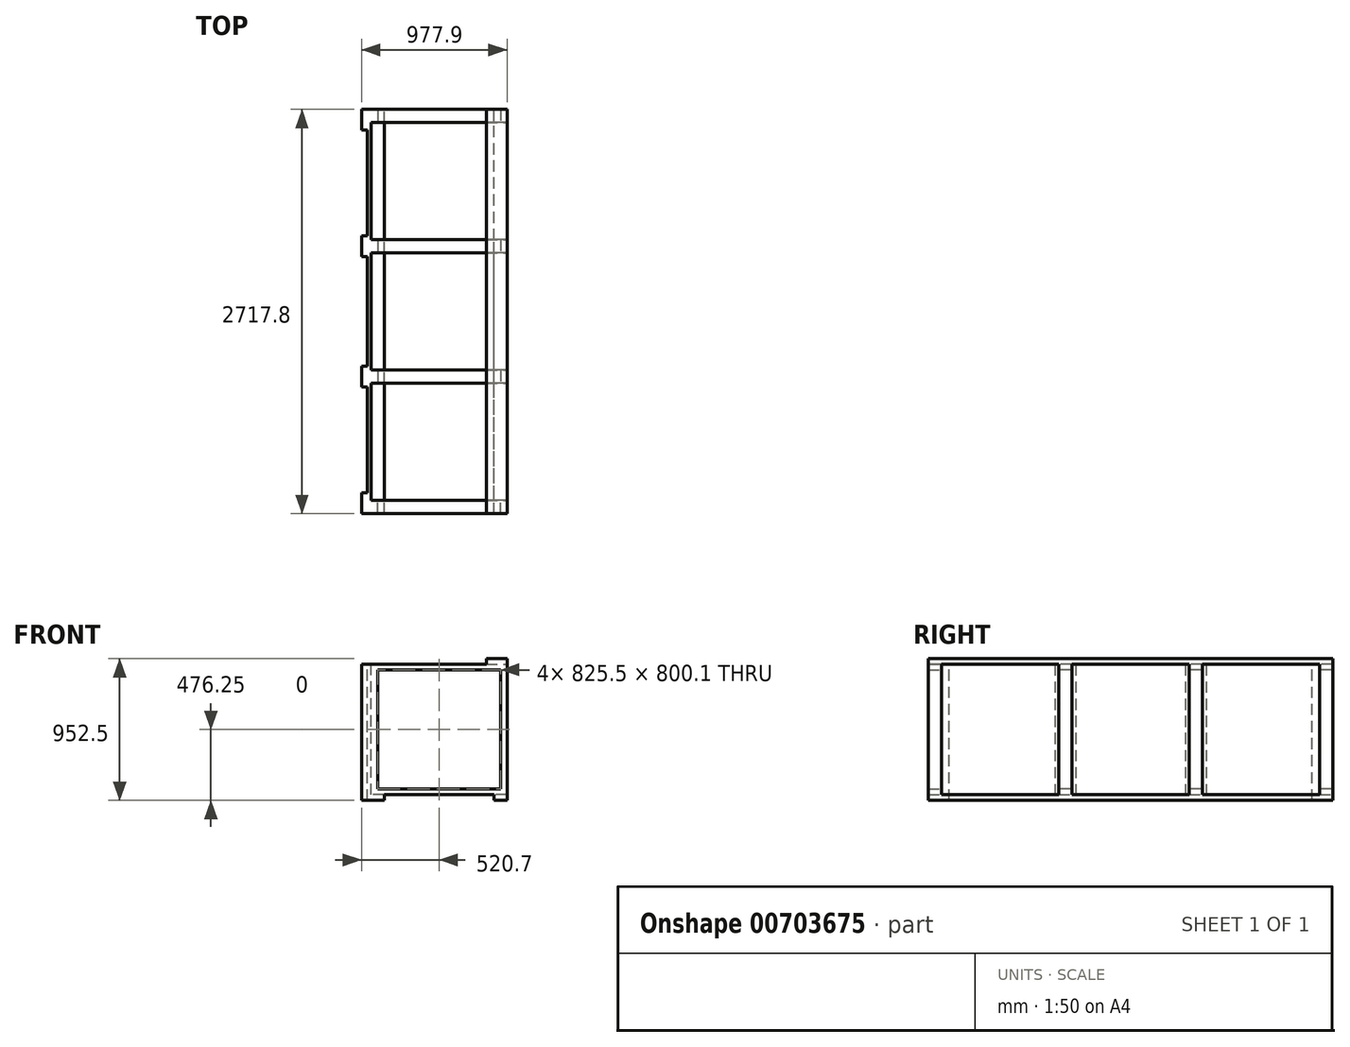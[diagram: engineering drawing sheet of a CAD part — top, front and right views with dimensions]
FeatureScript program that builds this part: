
annotation { "Feature Type Name" : "Feature", "Feature Type Description" : "" }
export const myFeature = defineFeature(function(context is Context, id is Id, definition is map)
    precondition{}
    {
        {
            var Q0;
            Q0=qCreatedBy(makeId("Front.planeOp"),FACE);
            var sketch = newSketch(context, id + "F0", { "sketchPlane" : qUnion([Q0])});
            skLineSegment(sketch, "E0.bottom", {"start": v(0, 0) * mm, "end": v(88.9, 0) * mm});
            skLineSegment(sketch, "E0.top", {"start": v(0, 76.2) * mm, "end": v(914.4, 76.2) * mm});
            skLineSegment(sketch, "E0.left", {"start": v(0, 0) * mm, "end": v(0, 76.2) * mm});
            skLineSegment(sketch, "E0.right", {"start": v(914.4, 0) * mm, "end": v(914.4, 76.2) * mm});
            skLineSegment(sketch, "E1.top", {"start": v(88.9, 38.1) * mm, "end": v(825.5, 38.1) * mm});
            skLineSegment(sketch, "E1.left", {"start": v(88.9, 0) * mm, "end": v(88.9, 38.1) * mm});
            skLineSegment(sketch, "E1.right", {"start": v(825.5, 0) * mm, "end": v(825.5, 38.1) * mm});
            skLineSegment(sketch, "E2.trimOffspring", {"start": v(825.5, 0) * mm, "end": v(914.4, 0) * mm});
            skSolve(sketch);
        }
        {
            var Q0;
            Q0=makeQuery(id+"F0.imprint","IMPRINT",FACE,{"disambiguationData":[TD([[makeQuery(id+"F0.imprint","IMPRINT",EDGE,{"derivedFrom":sQuery(id+"F0.wireOp",EDGE,"E0.bottom")}),1.0]])]});
            extrude(context, id + "F1", {"entities" : qUnion([Q0]), "depth" : 2717.8 * mm, "offsetDistance" : 25.4 * mm});
        }
        {
            var Q0;
            Q0=makeQuery(id+"F1.opExtrude","SWEPT_FACE",FACE,{"disambiguationData":[OSD([sQuery(id+"F0.wireOp",EDGE,"E0.top")])]});
            var sketch = newSketch(context, id + "F2", { "sketchPlane" : qUnion([Q0])});
            skLineSegment(sketch, "E3.bottom", {"start": v(914.4, -2628.9) * mm, "end": v(0, -2628.9) * mm});
            skLineSegment(sketch, "E3.top", {"start": v(914.4, -1841.5) * mm, "end": v(0, -1841.5) * mm});
            skLineSegment(sketch, "E3.left", {"start": v(914.4, -2628.9) * mm, "end": v(914.4, -1841.5) * mm});
            skLineSegment(sketch, "E3.right", {"start": v(0, -2628.9) * mm, "end": v(0, -1841.5) * mm});
            skLineSegment(sketch, "E4.bottom", {"start": v(914.4, -88.9) * mm, "end": v(0, -88.9) * mm});
            skLineSegment(sketch, "E4.top", {"start": v(914.4, -876.3) * mm, "end": v(0, -876.3) * mm});
            skLineSegment(sketch, "E4.left", {"start": v(914.4, -88.9) * mm, "end": v(914.4, -876.3) * mm});
            skLineSegment(sketch, "E4.right", {"start": v(0, -88.9) * mm, "end": v(0, -876.3) * mm});
            skLineSegment(sketch, "E5.bottom", {"start": v(914.4, -1752.6) * mm, "end": v(0, -1752.6) * mm});
            skLineSegment(sketch, "E5.top", {"start": v(914.4, -965.2) * mm, "end": v(0, -965.2) * mm});
            skLineSegment(sketch, "E5.left", {"start": v(914.4, -1752.6) * mm, "end": v(914.4, -965.2) * mm});
            skLineSegment(sketch, "E5.right", {"start": v(0, -1752.6) * mm, "end": v(0, -965.2) * mm});
            skSolve(sketch);
        }
        {
            var Q0;
            Q0=makeQuery(id+"F2.imprint","IMPRINT",FACE,{"disambiguationData":[TD([[makeQuery(id+"F2.imprint","IMPRINT",EDGE,{"derivedFrom":sQuery(id+"F2.wireOp",EDGE,"E3.bottom")}),-1.0]])]});
            var Q1;
            Q1=makeQuery(id+"F2.imprint","IMPRINT",FACE,{"disambiguationData":[TD([[makeQuery(id+"F2.imprint","IMPRINT",EDGE,{"derivedFrom":sQuery(id+"F2.wireOp",EDGE,"E5.bottom")}),-1.0]])]});
            var Q2;
            Q2=makeQuery(id+"F2.imprint","IMPRINT",FACE,{"disambiguationData":[TD([[makeQuery(id+"F2.imprint","IMPRINT",EDGE,{"derivedFrom":sQuery(id+"F2.wireOp",EDGE,"E4.bottom")}),1.0]])]});
            extrude(context, id + "F3", {"entities" : qUnion([Q0, Q1, Q2]), "operationType" : NewBodyOperationType.REMOVE, "oppositeDirection" : true, "depth" : 38.1 * mm, "offsetDistance" : 25.4 * mm});
        }
        {
            var Q0;
            {var subQ2=sQuery(id+"F0.wireOp",EDGE,"E0.top");Q0=makeQuery(id+"F3.boolean.opBoolean","SPLIT",FACE,{"disambiguationData":[TD([makeQuery(id+"F3.opExtrude","SWEPT_FACE",FACE,{"disambiguationData":[OSD([sQuery(id+"F2.wireOp",EDGE,"E4.bottom")])]})])],"derivedFrom":makeQuery(id+"F1.opExtrude","SWEPT_FACE",FACE,{"disambiguationData":[OSD([subQ2])]})});}
            var sketch = newSketch(context, id + "F4", { "sketchPlane" : qUnion([Q0])});
            skLineSegment(sketch, "E6", {"start": v(0, 0) * mm, "end": v(0, -2717.8) * mm, "construction": true});
            skLineSegment(sketch, "E7", {"start": v(914.4, 0) * mm, "end": v(914.4, -2717.8) * mm, "construction": true});
            skLineSegment(sketch, "E8", {"start": v(88.9, 0) * mm, "end": v(88.9, -2717.8) * mm, "construction": true});
            skLineSegment(sketch, "E9", {"start": v(825.5, 0) * mm, "end": v(825.5, -2717.8) * mm, "construction": true});
            skLineSegment(sketch, "E10.bottom", {"start": v(0, 0) * mm, "end": v(44.45, 0) * mm});
            skLineSegment(sketch, "E10.top", {"start": v(0, -88.9) * mm, "end": v(44.45, -88.9) * mm});
            skLineSegment(sketch, "E10.left", {"start": v(0, 0) * mm, "end": v(0, -88.9) * mm});
            skLineSegment(sketch, "E10.right", {"start": v(44.45, 0) * mm, "end": v(44.45, -88.9) * mm});
            skLineSegment(sketch, "E11.bottom", {"start": v(914.4, 0) * mm, "end": v(869.95, 0) * mm});
            skLineSegment(sketch, "E11.top", {"start": v(914.4, -88.9) * mm, "end": v(869.95, -88.9) * mm});
            skLineSegment(sketch, "E11.left", {"start": v(914.4, 0) * mm, "end": v(914.4, -88.9) * mm});
            skLineSegment(sketch, "E11.right", {"start": v(869.95, 0) * mm, "end": v(869.95, -88.9) * mm});
            skLineSegment(sketch, "E12", {"start": v(0, -2717.8) * mm, "end": v(914.4, -2717.8) * mm, "construction": true});
            skLineSegment(sketch, "E13", {"start": v(0, -2628.9) * mm, "end": v(914.4, -2628.9) * mm, "construction": true});
            skLineSegment(sketch, "E14", {"start": v(0, -1841.5) * mm, "end": v(914.4, -1841.5) * mm, "construction": true});
            skLineSegment(sketch, "E15", {"start": v(0, -1752.6) * mm, "end": v(914.4, -1752.6) * mm, "construction": true});
            skLineSegment(sketch, "E16", {"start": v(0, -965.2) * mm, "end": v(914.4, -965.2) * mm, "construction": true});
            skLineSegment(sketch, "E17", {"start": v(0, -876.3) * mm, "end": v(914.4, -876.3) * mm, "construction": true});
            skLineSegment(sketch, "E18.bottom", {"start": v(0, -876.3) * mm, "end": v(44.45, -876.3) * mm});
            skLineSegment(sketch, "E18.top", {"start": v(0, -965.2) * mm, "end": v(44.45, -965.2) * mm});
            skLineSegment(sketch, "E18.left", {"start": v(0, -876.3) * mm, "end": v(0, -965.2) * mm});
            skLineSegment(sketch, "E18.right", {"start": v(44.45, -876.3) * mm, "end": v(44.45, -965.2) * mm});
            skLineSegment(sketch, "E19.bottom", {"start": v(914.4, -876.3) * mm, "end": v(869.95, -876.3) * mm});
            skLineSegment(sketch, "E19.top", {"start": v(914.4, -965.2) * mm, "end": v(869.95, -965.2) * mm});
            skLineSegment(sketch, "E19.left", {"start": v(914.4, -876.3) * mm, "end": v(914.4, -965.2) * mm});
            skLineSegment(sketch, "E19.right", {"start": v(869.95, -876.3) * mm, "end": v(869.95, -965.2) * mm});
            skLineSegment(sketch, "E20.bottom", {"start": v(0, -1752.6) * mm, "end": v(44.45, -1752.6) * mm});
            skLineSegment(sketch, "E20.top", {"start": v(0, -1841.5) * mm, "end": v(44.45, -1841.5) * mm});
            skLineSegment(sketch, "E20.left", {"start": v(0, -1752.6) * mm, "end": v(0, -1841.5) * mm});
            skLineSegment(sketch, "E20.right", {"start": v(44.45, -1752.6) * mm, "end": v(44.45, -1841.5) * mm});
            skLineSegment(sketch, "E21.bottom", {"start": v(914.4, -1752.6) * mm, "end": v(869.95, -1752.6) * mm});
            skLineSegment(sketch, "E21.top", {"start": v(914.4, -1841.5) * mm, "end": v(869.95, -1841.5) * mm});
            skLineSegment(sketch, "E21.left", {"start": v(914.4, -1752.6) * mm, "end": v(914.4, -1841.5) * mm});
            skLineSegment(sketch, "E21.right", {"start": v(869.95, -1752.6) * mm, "end": v(869.95, -1841.5) * mm});
            skLineSegment(sketch, "E22.bottom", {"start": v(0, -2717.8) * mm, "end": v(44.45, -2717.8) * mm});
            skLineSegment(sketch, "E22.top", {"start": v(0, -2628.9) * mm, "end": v(44.45, -2628.9) * mm});
            skLineSegment(sketch, "E22.left", {"start": v(0, -2717.8) * mm, "end": v(0, -2628.9) * mm});
            skLineSegment(sketch, "E22.right", {"start": v(44.45, -2717.8) * mm, "end": v(44.45, -2628.9) * mm});
            skLineSegment(sketch, "E23.bottom", {"start": v(914.4, -2717.8) * mm, "end": v(869.95, -2717.8) * mm});
            skLineSegment(sketch, "E23.top", {"start": v(914.4, -2628.9) * mm, "end": v(869.95, -2628.9) * mm});
            skLineSegment(sketch, "E23.left", {"start": v(914.4, -2717.8) * mm, "end": v(914.4, -2628.9) * mm});
            skLineSegment(sketch, "E23.right", {"start": v(869.95, -2717.8) * mm, "end": v(869.95, -2628.9) * mm});
            skSolve(sketch);
        }
        {
            var Q0;
            Q0=makeQuery(id+"F4.imprint","IMPRINT",FACE,{"disambiguationData":[TD([[makeQuery(id+"F4.imprint","IMPRINT",EDGE,{"derivedFrom":sQuery(id+"F4.wireOp",EDGE,"E11.bottom")}),-1.0]])]});
            var Q1;
            Q1=makeQuery(id+"F4.imprint","IMPRINT",FACE,{"disambiguationData":[TD([[makeQuery(id+"F4.imprint","IMPRINT",EDGE,{"derivedFrom":sQuery(id+"F4.wireOp",EDGE,"E10.bottom")}),-1.0]])]});
            var Q2;
            Q2=makeQuery(id+"F4.imprint","IMPRINT",FACE,{"disambiguationData":[TD([[makeQuery(id+"F4.imprint","IMPRINT",EDGE,{"derivedFrom":sQuery(id+"F4.wireOp",EDGE,"E18.bottom")}),-1.0]])]});
            var Q3;
            Q3=makeQuery(id+"F4.imprint","IMPRINT",FACE,{"disambiguationData":[TD([[makeQuery(id+"F4.imprint","IMPRINT",EDGE,{"derivedFrom":sQuery(id+"F4.wireOp",EDGE,"E19.bottom")}),1.0]])]});
            var Q4;
            Q4=makeQuery(id+"F4.imprint","IMPRINT",FACE,{"disambiguationData":[TD([[makeQuery(id+"F4.imprint","IMPRINT",EDGE,{"derivedFrom":sQuery(id+"F4.wireOp",EDGE,"E21.bottom")}),1.0]])]});
            var Q5;
            Q5=makeQuery(id+"F4.imprint","IMPRINT",FACE,{"disambiguationData":[TD([[makeQuery(id+"F4.imprint","IMPRINT",EDGE,{"derivedFrom":sQuery(id+"F4.wireOp",EDGE,"E20.bottom")}),-1.0]])]});
            var Q6;
            Q6=makeQuery(id+"F4.imprint","IMPRINT",FACE,{"disambiguationData":[TD([[makeQuery(id+"F4.imprint","IMPRINT",EDGE,{"derivedFrom":sQuery(id+"F4.wireOp",EDGE,"E22.bottom")}),1.0]])]});
            var Q7;
            Q7=makeQuery(id+"F4.imprint","IMPRINT",FACE,{"disambiguationData":[TD([[makeQuery(id+"F4.imprint","IMPRINT",EDGE,{"derivedFrom":sQuery(id+"F4.wireOp",EDGE,"E23.bottom")}),-1.0]])]});
            extrude(context, id + "F5", {"entities" : qUnion([Q0, Q1, Q2, Q3, Q4, Q5, Q6, Q7]), "operationType" : NewBodyOperationType.ADD, "depth" : 800.1 * mm, "offsetDistance" : 25.4 * mm});
        }
        {
            var Q0;
            Q0=makeQuery(id+"F5.boolean.opBoolean","MERGE",FACE,{"derivedFrom":[makeQuery(id+"F1.opExtrude","SWEPT_FACE",FACE,{"disambiguationData":[OSD([sQuery(id+"F0.wireOp",EDGE,"E0.right")])]}),makeQuery(id+"F5.opExtrude","SWEPT_FACE",FACE,{"disambiguationData":[OSD([sQuery(id+"F4.wireOp",EDGE,"E11.left")])]}),makeQuery(id+"F5.opExtrude","SWEPT_FACE",FACE,{"disambiguationData":[OSD([sQuery(id+"F4.wireOp",EDGE,"E19.left")])]}),makeQuery(id+"F5.opExtrude","SWEPT_FACE",FACE,{"disambiguationData":[OSD([sQuery(id+"F4.wireOp",EDGE,"E21.left")])]}),makeQuery(id+"F5.opExtrude","SWEPT_FACE",FACE,{"disambiguationData":[OSD([sQuery(id+"F4.wireOp",EDGE,"E23.left")])]})]});
            var sketch = newSketch(context, id + "F6", { "sketchPlane" : qUnion([Q0])});
            skLineSegment(sketch, "E24.bottom", {"start": v(-2717.8, 876.3) * mm, "end": v(-2628.9, 876.3) * mm});
            skLineSegment(sketch, "E24.top", {"start": v(-2717.8, 914.4) * mm, "end": v(-2628.9, 914.4) * mm});
            skLineSegment(sketch, "E24.left", {"start": v(-2717.8, 876.3) * mm, "end": v(-2717.8, 914.4) * mm});
            skLineSegment(sketch, "E24.right", {"start": v(-2628.9, 876.3) * mm, "end": v(-2628.9, 914.4) * mm});
            skLineSegment(sketch, "E25.bottom", {"start": v(-1841.5, 876.3) * mm, "end": v(-1752.6, 876.3) * mm});
            skLineSegment(sketch, "E25.top", {"start": v(-1841.5, 914.4) * mm, "end": v(-1752.6, 914.4) * mm});
            skLineSegment(sketch, "E25.left", {"start": v(-1841.5, 876.3) * mm, "end": v(-1841.5, 914.4) * mm});
            skLineSegment(sketch, "E25.right", {"start": v(-1752.6, 876.3) * mm, "end": v(-1752.6, 914.4) * mm});
            skLineSegment(sketch, "E26.bottom", {"start": v(-965.2, 876.3) * mm, "end": v(-876.3, 876.3) * mm});
            skLineSegment(sketch, "E26.top", {"start": v(-965.2, 914.4) * mm, "end": v(-876.3, 914.4) * mm});
            skLineSegment(sketch, "E26.left", {"start": v(-965.2, 876.3) * mm, "end": v(-965.2, 914.4) * mm});
            skLineSegment(sketch, "E26.right", {"start": v(-876.3, 876.3) * mm, "end": v(-876.3, 914.4) * mm});
            skLineSegment(sketch, "E27.bottom", {"start": v(-88.9, 876.3) * mm, "end": v(0, 876.3) * mm});
            skLineSegment(sketch, "E27.top", {"start": v(-88.9, 914.4) * mm, "end": v(0, 914.4) * mm});
            skLineSegment(sketch, "E27.left", {"start": v(-88.9, 876.3) * mm, "end": v(-88.9, 914.4) * mm});
            skLineSegment(sketch, "E27.right", {"start": v(0, 876.3) * mm, "end": v(0, 914.4) * mm});
            skSolve(sketch);
        }
        {
            var Q0;
            Q0=makeQuery(id+"F6.imprint","IMPRINT",FACE,{"disambiguationData":[TD([[makeQuery(id+"F6.imprint","IMPRINT",EDGE,{"derivedFrom":sQuery(id+"F6.wireOp",EDGE,"E24.bottom")}),1.0]])]});
            var Q1;
            Q1=makeQuery(id+"F6.imprint","IMPRINT",FACE,{"disambiguationData":[TD([[makeQuery(id+"F6.imprint","IMPRINT",EDGE,{"derivedFrom":sQuery(id+"F6.wireOp",EDGE,"E25.bottom")}),-1.0]])]});
            var Q2;
            Q2=makeQuery(id+"F6.imprint","IMPRINT",FACE,{"disambiguationData":[TD([[makeQuery(id+"F6.imprint","IMPRINT",EDGE,{"derivedFrom":sQuery(id+"F6.wireOp",EDGE,"E26.bottom")}),-1.0]])]});
            var Q3;
            Q3=makeQuery(id+"F6.imprint","IMPRINT",FACE,{"disambiguationData":[TD([[makeQuery(id+"F6.imprint","IMPRINT",EDGE,{"derivedFrom":sQuery(id+"F6.wireOp",EDGE,"E27.bottom")}),1.0]])]});
            extrude(context, id + "F7", {"entities" : qUnion([Q0, Q1, Q2, Q3]), "operationType" : NewBodyOperationType.ADD, "oppositeDirection" : true, "depth" : 914.4 * mm, "offsetDistance" : 25.4 * mm});
        }
        {
            var Q0;
            Q0=makeQuery(id+"F7.boolean.opBoolean","MERGE",FACE,{"derivedFrom":[makeQuery(id+"F5.boolean.opBoolean","MERGE",FACE,{"derivedFrom":[makeQuery(id+"F1.opExtrude","CAP_FACE",FACE,{"disambiguationData":[OSD([sQuery(id+"F0.wireOp",EDGE,"E0.bottom"),sQuery(id+"F0.wireOp",EDGE,"E0.top"),sQuery(id+"F0.wireOp",EDGE,"E0.left"),sQuery(id+"F0.wireOp",EDGE,"E0.right"),sQuery(id+"F0.wireOp",EDGE,"E1.top"),sQuery(id+"F0.wireOp",EDGE,"E1.left"),sQuery(id+"F0.wireOp",EDGE,"E1.right"),sQuery(id+"F0.wireOp",EDGE,"E2.trimOffspring")])],"isStart":false}),makeQuery(id+"F5.opExtrude","SWEPT_FACE",FACE,{"disambiguationData":[OSD([sQuery(id+"F4.wireOp",EDGE,"E22.bottom")])]}),makeQuery(id+"F5.opExtrude","SWEPT_FACE",FACE,{"disambiguationData":[OSD([sQuery(id+"F4.wireOp",EDGE,"E23.bottom")])]})]}),makeQuery(id+"F7.opExtrude","SWEPT_FACE",FACE,{"disambiguationData":[OSD([sQuery(id+"F6.wireOp",EDGE,"E24.left")])]})]});
            var sketch = newSketch(context, id + "F8", { "sketchPlane" : qUnion([Q0])});
            skLineSegment(sketch, "E28.bottom", {"start": v(914.4, 914.4) * mm, "end": v(774.7, 914.4) * mm});
            skLineSegment(sketch, "E28.top", {"start": v(914.4, 952.5) * mm, "end": v(774.7, 952.5) * mm});
            skLineSegment(sketch, "E28.left", {"start": v(914.4, 914.4) * mm, "end": v(914.4, 952.5) * mm});
            skLineSegment(sketch, "E28.right", {"start": v(774.7, 914.4) * mm, "end": v(774.7, 952.5) * mm});
            skSolve(sketch);
        }
        {
            var Q0;
            Q0=makeQuery(id+"F8.imprint","IMPRINT",FACE,{"disambiguationData":[TD([[makeQuery(id+"F8.imprint","IMPRINT",EDGE,{"derivedFrom":sQuery(id+"F8.wireOp",EDGE,"E28.bottom")}),1.0]])]});
            extrude(context, id + "F9", {"entities" : qUnion([Q0]), "operationType" : NewBodyOperationType.ADD, "oppositeDirection" : true, "depth" : 2717.8 * mm, "offsetDistance" : 25.4 * mm});
        }
        {
            var Q0;
            Q0=makeQuery(id+"F7.boolean.opBoolean","MERGE",FACE,{"derivedFrom":[makeQuery(id+"F5.boolean.opBoolean","MERGE",FACE,{"derivedFrom":[makeQuery(id+"F1.opExtrude","SWEPT_FACE",FACE,{"disambiguationData":[OSD([sQuery(id+"F0.wireOp",EDGE,"E0.left")])]}),makeQuery(id+"F5.opExtrude","SWEPT_FACE",FACE,{"disambiguationData":[OSD([sQuery(id+"F4.wireOp",EDGE,"E10.left")])]}),makeQuery(id+"F5.opExtrude","SWEPT_FACE",FACE,{"disambiguationData":[OSD([sQuery(id+"F4.wireOp",EDGE,"E18.left")])]}),makeQuery(id+"F5.opExtrude","SWEPT_FACE",FACE,{"disambiguationData":[OSD([sQuery(id+"F4.wireOp",EDGE,"E20.left")])]}),makeQuery(id+"F5.opExtrude","SWEPT_FACE",FACE,{"disambiguationData":[OSD([sQuery(id+"F4.wireOp",EDGE,"E22.left")])]})]}),makeQuery(id+"F7.opExtrude","CAP_FACE",FACE,{"disambiguationData":[OSD([sQuery(id+"F6.wireOp",EDGE,"E24.bottom"),sQuery(id+"F6.wireOp",EDGE,"E24.top"),sQuery(id+"F6.wireOp",EDGE,"E24.left"),sQuery(id+"F6.wireOp",EDGE,"E24.right")])],"isStart":false}),makeQuery(id+"F7.opExtrude","CAP_FACE",FACE,{"disambiguationData":[OSD([sQuery(id+"F6.wireOp",EDGE,"E25.bottom"),sQuery(id+"F6.wireOp",EDGE,"E25.top"),sQuery(id+"F6.wireOp",EDGE,"E25.left"),sQuery(id+"F6.wireOp",EDGE,"E25.right")])],"isStart":false}),makeQuery(id+"F7.opExtrude","CAP_FACE",FACE,{"disambiguationData":[OSD([sQuery(id+"F6.wireOp",EDGE,"E26.bottom"),sQuery(id+"F6.wireOp",EDGE,"E26.top"),sQuery(id+"F6.wireOp",EDGE,"E26.left"),sQuery(id+"F6.wireOp",EDGE,"E26.right")])],"isStart":false}),makeQuery(id+"F7.opExtrude","CAP_FACE",FACE,{"disambiguationData":[OSD([sQuery(id+"F6.wireOp",EDGE,"E27.bottom"),sQuery(id+"F6.wireOp",EDGE,"E27.top"),sQuery(id+"F6.wireOp",EDGE,"E27.left"),sQuery(id+"F6.wireOp",EDGE,"E27.right")])],"isStart":false})]});
            var sketch = newSketch(context, id + "F10", { "sketchPlane" : qUnion([Q0])});
            skLineSegment(sketch, "E29.bottom", {"start": v(0, 0) * mm, "end": v(139.7, 0) * mm});
            skLineSegment(sketch, "E29.top", {"start": v(0, 914.4) * mm, "end": v(139.7, 914.4) * mm});
            skLineSegment(sketch, "E29.left", {"start": v(0, 0) * mm, "end": v(0, 914.4) * mm});
            skLineSegment(sketch, "E29.right", {"start": v(139.7, 0) * mm, "end": v(139.7, 914.4) * mm});
            skLineSegment(sketch, "E30.bottom", {"start": v(2717.8, 0) * mm, "end": v(2578.1, 0) * mm});
            skLineSegment(sketch, "E30.top", {"start": v(2717.8, 914.4) * mm, "end": v(2578.1, 914.4) * mm});
            skLineSegment(sketch, "E30.left", {"start": v(2717.8, 0) * mm, "end": v(2717.8, 914.4) * mm});
            skLineSegment(sketch, "E30.right", {"start": v(2578.1, 0) * mm, "end": v(2578.1, 914.4) * mm});
            skLineSegment(sketch, "E31.bottom", {"start": v(850.9, 914.4) * mm, "end": v(990.6, 914.4) * mm});
            skLineSegment(sketch, "E31.top", {"start": v(850.9, 0) * mm, "end": v(990.6, 0) * mm});
            skLineSegment(sketch, "E31.left", {"start": v(850.9, 914.4) * mm, "end": v(850.9, 0) * mm});
            skLineSegment(sketch, "E31.right", {"start": v(990.6, 914.4) * mm, "end": v(990.6, 0) * mm});
            skLineSegment(sketch, "E32.bottom", {"start": v(1727.2, 914.4) * mm, "end": v(1866.9, 914.4) * mm});
            skLineSegment(sketch, "E32.top", {"start": v(1727.2, 0) * mm, "end": v(1866.9, 0) * mm});
            skLineSegment(sketch, "E32.left", {"start": v(1727.2, 914.4) * mm, "end": v(1727.2, 0) * mm});
            skLineSegment(sketch, "E32.right", {"start": v(1866.9, 914.4) * mm, "end": v(1866.9, 0) * mm});
            skSolve(sketch);
        }
        {
            var Q0;
            Q0 = qSketchRegion(id + "F10", true);
            extrude(context, id + "F11", {"entities" : qUnion([Q0]), "operationType" : NewBodyOperationType.ADD, "depth" : 63.5 * mm, "offsetDistance" : 25.4 * mm});
        }
        {
            var Q0;
            Q0=makeQuery(id+"F11.boolean.opBoolean","MERGE",FACE,{"derivedFrom":[makeQuery(id+"F7.opExtrude","SWEPT_FACE",FACE,{"disambiguationData":[OSD([sQuery(id+"F6.wireOp",EDGE,"E27.top")])]}),makeQuery(id+"F11.opExtrude","SWEPT_FACE",FACE,{"disambiguationData":[OSD([sQuery(id+"F10.wireOp",EDGE,"E29.top")])]})]});
            var sketch = newSketch(context, id + "F12", { "sketchPlane" : qUnion([Q0])});
            skLineSegment(sketch, "E33.bottom", {"start": v(0, 0) * mm, "end": v(-25.4, 0) * mm});
            skLineSegment(sketch, "E33.top", {"start": v(0, -2717.8) * mm, "end": v(-25.4, -2717.8) * mm});
            skLineSegment(sketch, "E33.left", {"start": v(0, 0) * mm, "end": v(0, -2717.8) * mm});
            skLineSegment(sketch, "E33.right", {"start": v(-25.4, 0) * mm, "end": v(-25.4, -2717.8) * mm});
            skSolve(sketch);
        }
        {
            var Q0;
            Q0 = qSketchRegion(id + "F12", true);
            extrude(context, id + "F13", {"entities" : qUnion([Q0]), "operationType" : NewBodyOperationType.ADD, "oppositeDirection" : true, "depth" : 914.4 * mm, "offsetDistance" : 25.4 * mm});
        }
    });
